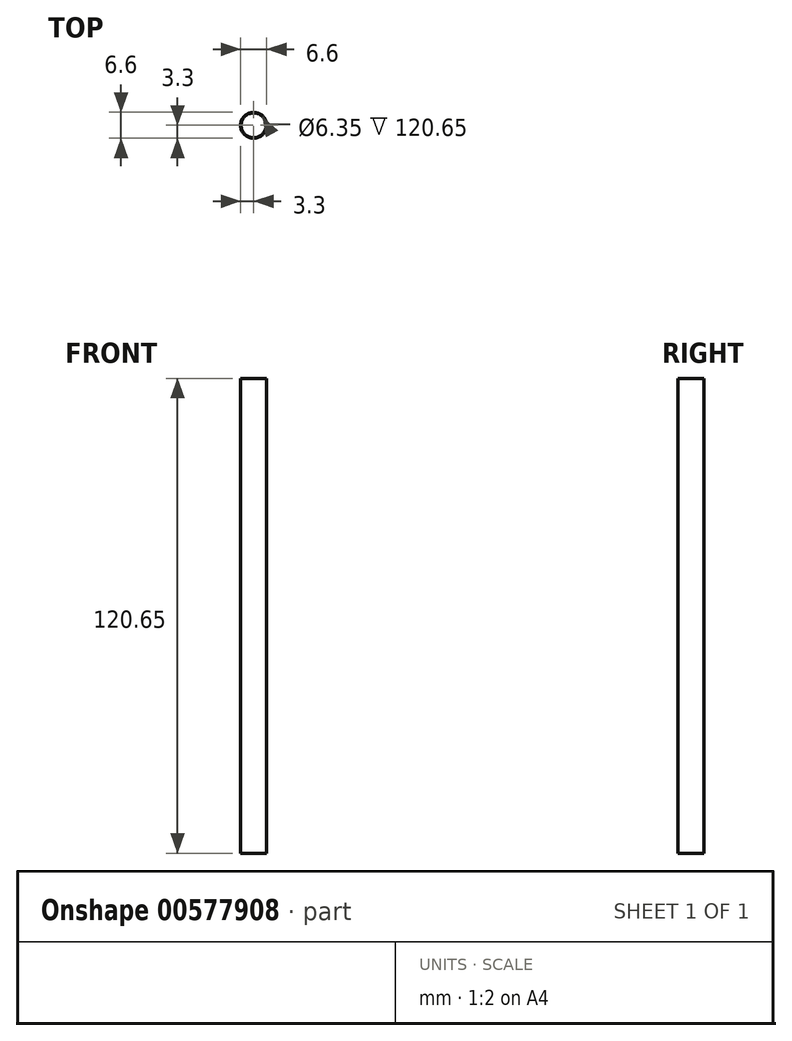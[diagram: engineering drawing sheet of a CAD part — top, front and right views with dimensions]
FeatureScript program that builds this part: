
annotation { "Feature Type Name" : "Feature", "Feature Type Description" : "" }
export const myFeature = defineFeature(function(context is Context, id is Id, definition is map)
    precondition{}
    {
        {
            var Q0;
            Q0=qCreatedBy(makeId("Top.planeOp"),FACE);
            var sketch = newSketch(context, id + "F0", { "sketchPlane" : qUnion([Q0])});
            skCircle(sketch, "E0", {"center": v(0, 0) * mm, "radius": 3.18 * mm});
            skCircle(sketch, "E1", {"center": v(0, 0) * mm, "radius": 3.3 * mm});
            skSolve(sketch);
        }
        {
            var Q0;
            Q0 = qSketchRegion(id + "F0", true);
            extrude(context, id + "F1", {"entities" : qUnion([Q0]), "depth" : 120.65 * mm, "offsetDistance" : 25.4 * mm});
        }
    });
